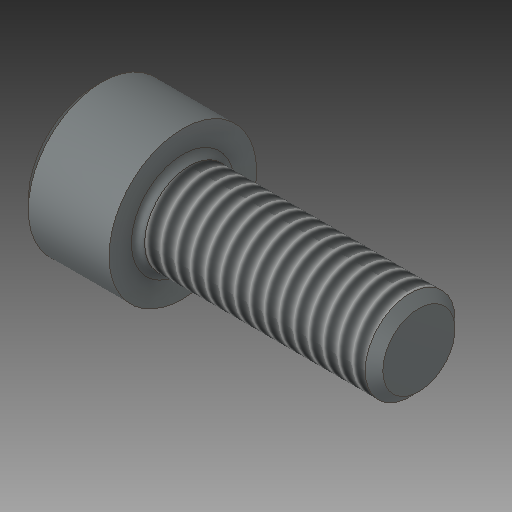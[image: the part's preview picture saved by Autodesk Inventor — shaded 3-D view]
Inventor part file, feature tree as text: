
AUTODESK INVENTOR PART (.ipt)
format: ipt  version: 2018 (Build 220112000, 112)  size: 196,096 bytes
history: native  units: in
note: dims shown in document units (in); Inventor stores cm internally (conversion verified against a paired STEP export)
features: thread x1, other x1
ambient origin geometry x8: Origin, YZ Plane, XZ Plane, XY Plane, X Axis, Y Axis, Z Axis, Center Point
bodies: Solid1 (feature_tree)
feature tree (2):
  thread  "Thread1"  [1 undecoded]
  other  "Hex"
note: 1 required parameter value undecoded (feature->parameter linkage not recoverable at this tier; creation-order binding heuristic only, values carry confidence <= 0.55)
